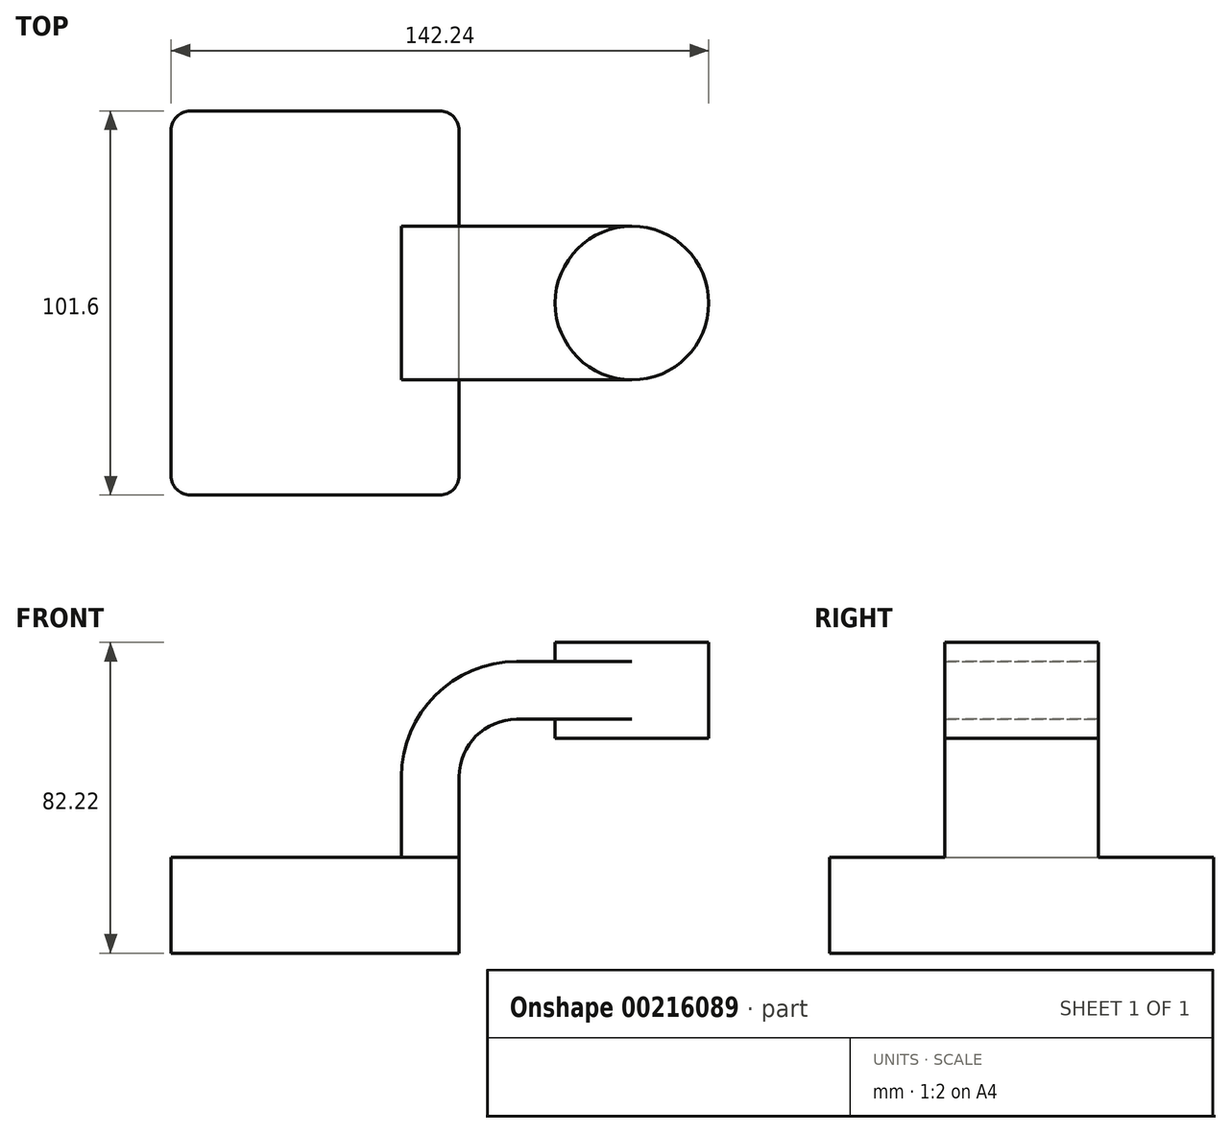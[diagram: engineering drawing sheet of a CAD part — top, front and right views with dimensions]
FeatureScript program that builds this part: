
annotation { "Feature Type Name" : "Feature", "Feature Type Description" : "" }
export const myFeature = defineFeature(function(context is Context, id is Id, definition is map)
    precondition{}
    {
        {
            var Q0;
            Q0=qCreatedBy(makeId("Front.planeOp"),FACE);
            var sketch = newSketch(context, id + "F0", { "sketchPlane" : qUnion([Q0])});
            skLineSegment(sketch, "E0.bottom", {"start": v(38.1, -12.7) * mm, "end": v(-38.1, -12.7) * mm});
            skLineSegment(sketch, "E0.top", {"start": v(38.1, 12.7) * mm, "end": v(-38.1, 12.7) * mm});
            skLineSegment(sketch, "E0.left", {"start": v(38.1, -12.7) * mm, "end": v(38.1, 12.7) * mm});
            skLineSegment(sketch, "E0.right", {"start": v(-38.1, -12.7) * mm, "end": v(-38.1, 12.7) * mm});
            skPoint(sketch, "E0.middle", {"position": v(0, 0) * mm});
            skLineSegment(sketch, "E1", {"start": v(38.1, 12.7) * mm, "end": v(38.1, 33.96) * mm});
            skArc(sketch, "E2", {"start": v(38.1, 33.96) * mm, "mid": v(42.56, 44.74) * mm, "end": v(53.34, 49.2) * mm});
            skLineSegment(sketch, "E3", {"start": v(53.34, 49.2) * mm, "end": v(83.82, 49.2) * mm});
            skLineSegment(sketch, "E4.0", {"start": v(53.34, 64.44) * mm, "end": v(83.82, 64.44) * mm});
            skArc(sketch, "E4.1", {"start": v(22.86, 33.96) * mm, "mid": v(31.79, 55.51) * mm, "end": v(53.34, 64.44) * mm});
            skLineSegment(sketch, "E4.2", {"start": v(22.86, 12.7) * mm, "end": v(22.86, 33.96) * mm});
            skLineSegment(sketch, "E5", {"start": v(83.82, 102.97) * mm, "end": v(83.82, 23.35) * mm});
            skPoint(sketch, "E6.middle", {"position": v(83.82, 49.2) * mm});
            skLineSegment(sketch, "E7.bottom", {"start": v(63.5, 69.52) * mm, "end": v(104.14, 69.52) * mm});
            skLineSegment(sketch, "E7.top", {"start": v(63.5, 44.12) * mm, "end": v(104.14, 44.12) * mm});
            skLineSegment(sketch, "E7.left", {"start": v(63.5, 69.52) * mm, "end": v(63.5, 44.12) * mm});
            skLineSegment(sketch, "E7.right", {"start": v(104.14, 69.52) * mm, "end": v(104.14, 44.12) * mm});
            skPoint(sketch, "E8.orphan", {"position": v(109.9, 0) * mm});
            skFitSpline(sketch, "E9", {"points": [v(53.34, 64.44) * mm, v(-38.1, 12.7) * mm], "startDerivative": vector(-106.01, 4.34) * mm, "endDerivative": vector(-83.43, -79.1) * mm});
            skSolve(sketch);
        }
        {
            var Q0;
            {var subQ0=sQuery(id+"F0.wireOp",EDGE,"E5");var subQ1=sQuery(id+"F0.wireOp",EDGE,"E3");var subQ2=makeQuery(id+"F0.imprint","INTERSECT",VERTEX,{"derivedFrom":[subQ1,subQ0]});Q0=makeQuery(id+"F0.imprint","IMPRINT",FACE,{"disambiguationData":[TD([[makeQuery(id+"F0.imprint","IMPRINT",EDGE,{"disambiguationData":[TD([[subQ2,1.0]])],"derivedFrom":subQ1}),1.0]])]});}
            var Q1;
            {var subQ0=sQuery(id+"F0.wireOp",EDGE,"E5");var subQ1=sQuery(id+"F0.wireOp",EDGE,"E4.0");var subQ2=makeQuery(id+"F0.imprint","INTERSECT",VERTEX,{"derivedFrom":[subQ1,subQ0]});Q1=makeQuery(id+"F0.imprint","IMPRINT",FACE,{"disambiguationData":[TD([[makeQuery(id+"F0.imprint","IMPRINT",EDGE,{"disambiguationData":[TD([[subQ2,1.0]])],"derivedFrom":subQ1}),1.0]])]});}
            var Q2;
            {var subQ0=sQuery(id+"F0.wireOp",EDGE,"E5");var subQ1=sQuery(id+"F0.wireOp",EDGE,"E3");var subQ2=makeQuery(id+"F0.imprint","INTERSECT",VERTEX,{"derivedFrom":[subQ1,subQ0]});Q2=makeQuery(id+"F0.imprint","IMPRINT",FACE,{"disambiguationData":[TD([[makeQuery(id+"F0.imprint","IMPRINT",EDGE,{"disambiguationData":[TD([[subQ2,1.0]])],"derivedFrom":subQ1}),-1.0]])]});}
            var Q3;
            Q3=sQuery(id+"F0.wireOp",EDGE,"E5");
            revolve(context, id + "F1", {"entities" : qUnion([Q0, Q1, Q2]), "axis" : qUnion([Q3]), "revolveType" : RevolveType.FULL});
        }
        {
            var Q0;
            Q0=makeQuery(id+"F0.imprint","IMPRINT",FACE,{"disambiguationData":[TD([[makeQuery(id+"F0.imprint","IMPRINT",EDGE,{"derivedFrom":sQuery(id+"F0.wireOp",EDGE,"E0.bottom")}),-1.0]])]});
            extrude(context, id + "F2", {"entities" : qUnion([Q0]), "depth" : 50.8 * mm, "hasSecondDirection" : true, "secondDirectionOppositeDirection" : true, "secondDirectionDepth" : 50.8 * mm});
        }
        {
            var Q0;
            {var subQ0=sQuery(id+"F0.wireOp",EDGE,"E5");var subQ1=sQuery(id+"F0.wireOp",EDGE,"E3");var subQ2=makeQuery(id+"F0.imprint","INTERSECT",VERTEX,{"derivedFrom":[subQ1,subQ0]});Q0=makeQuery(id+"F0.imprint","IMPRINT",FACE,{"disambiguationData":[TD([[makeQuery(id+"F0.imprint","IMPRINT",EDGE,{"disambiguationData":[TD([[subQ2,1.0]])],"derivedFrom":subQ1}),1.0]])]});}
            var Q1;
            {var subQ4=sQuery(id+"F0.wireOp",EDGE,"E1");Q1=makeQuery(id+"F0.imprint","IMPRINT",FACE,{"disambiguationData":[TD([[makeQuery(id+"F0.imprint","IMPRINT",EDGE,{"derivedFrom":subQ4}),1.0]])]});}
            extrude(context, id + "F3", {"entities" : qUnion([Q0, Q1]), "operationType" : NewBodyOperationType.ADD, "depth" : 20.32 * mm, "hasSecondDirection" : true, "secondDirectionOppositeDirection" : true, "secondDirectionDepth" : 20.32 * mm});
        }
        {
            var Q0;
            Q0=makeQuery(id+"F0.imprint","IMPRINT",FACE,{"disambiguationData":[TD([[makeQuery(id+"F0.imprint","IMPRINT",EDGE,{"derivedFrom":sQuery(id+"F0.wireOp",EDGE,"E4.1")}),1.0]])]});
            extrude(context, id + "F4", {"entities" : qUnion([Q0]), "operationType" : NewBodyOperationType.ADD, "depth" : 7.62 * mm, "hasSecondDirection" : true, "secondDirectionOppositeDirection" : true, "secondDirectionDepth" : 7.62 * mm});
        }
        {
            var Q0;
            Q0=makeQuery(id+"F2.opExtrude","CAP_EDGE",EDGE,{"disambiguationData":[OSD([sQuery(id+"F0.wireOp",EDGE,"E0.right")])],"isStart":false});
            var Q1;
            Q1=makeQuery(id+"F2.opExtrude","CAP_EDGE",EDGE,{"disambiguationData":[OSD([sQuery(id+"F0.wireOp",EDGE,"E0.left")])],"isStart":false});
            var Q2;
            Q2=makeQuery(id+"F2.opExtrude","CAP_EDGE",EDGE,{"disambiguationData":[OSD([sQuery(id+"F0.wireOp",EDGE,"E0.right")])],"isStart":true});
            var Q3;
            Q3=makeQuery(id+"F2.opExtrude","CAP_EDGE",EDGE,{"disambiguationData":[OSD([sQuery(id+"F0.wireOp",EDGE,"E0.left")])],"isStart":true});
            fillet(context, id + "F5", {"entities" : qUnion([Q0, Q1, Q2, Q3]), "radius" : 5.08 * mm, "tangentPropagation" : true, "allowEdgeOverflow" : false});
        }
    });
